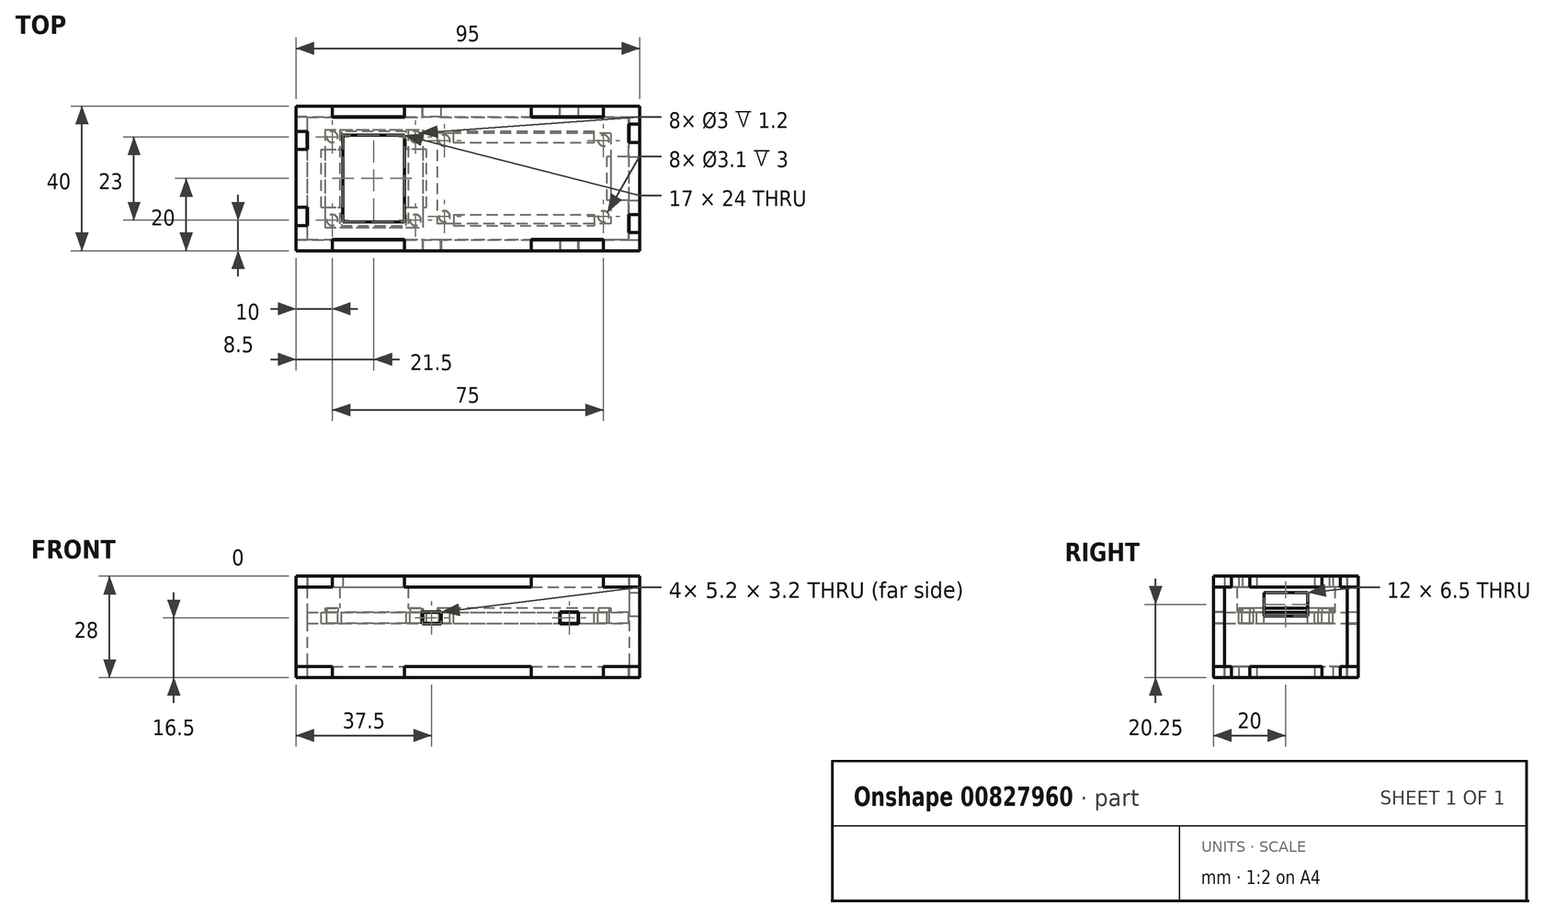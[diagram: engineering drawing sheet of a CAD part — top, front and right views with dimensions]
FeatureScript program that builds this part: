
annotation { "Feature Type Name" : "Feature", "Feature Type Description" : "" }
export const myFeature = defineFeature(function(context is Context, id is Id, definition is map)
    precondition{}
    {
        {
            var Q0;
            Q0=qCreatedBy(makeId("Top.planeOp"),FACE);
            var sketch = newSketch(context, id + "F0", { "sketchPlane" : qUnion([Q0])});
            skLineSegment(sketch, "E0.bottom", {"start": v(24, 12.5) * mm, "end": v(-24, 12.5) * mm});
            skLineSegment(sketch, "E0.top", {"start": v(24, -12.5) * mm, "end": v(-24, -12.5) * mm});
            skLineSegment(sketch, "E0.left", {"start": v(24, 12.5) * mm, "end": v(24, -12.5) * mm});
            skLineSegment(sketch, "E0.right", {"start": v(-24, 12.5) * mm, "end": v(-24, -12.5) * mm});
            skCircle(sketch, "E1", {"center": v(22, 10.5) * mm, "radius": 1.5 * mm});
            skCircle(sketch, "E2.MirrorC", {"center": v(22, -10.5) * mm, "radius": 1.5 * mm});
            skCircle(sketch, "E3.MirrorC", {"center": v(-22, 10.5) * mm, "radius": 1.5 * mm});
            skCircle(sketch, "E4.MirrorC", {"center": v(-22, -10.5) * mm, "radius": 1.5 * mm});
            skSolve(sketch);
        }
        {
            var Q0;
            Q0=makeQuery(id+"F0.imprint","IMPRINT",FACE,{"disambiguationData":[TD([[makeQuery(id+"F0.imprint","IMPRINT",EDGE,{"derivedFrom":sQuery(id+"F0.wireOp",EDGE,"E0.bottom")}),1.0]])]});
            extrude(context, id + "F1", {"entities" : qUnion([Q0]), "depth" : 1.2 * mm, "offsetDistance" : 25 * mm});
        }
        {
            var Q0;
            Q0=qCreatedBy(makeId("Top.planeOp"),FACE);
            cPlane(context, id + "F2", {"entities" : qUnion([Q0]), "cplaneType" : CPlaneType.OFFSET, "offset" : 0 * mm, "width" : 150 * mm, "height" : 150 * mm});
        }
        {
            var Q0;
            Q0=qCreatedBy(id+"F2.planeOp",FACE);
            var sketch = newSketch(context, id + "F3", { "sketchPlane" : qUnion([Q0])});
            skLineSegment(sketch, "E5.bottom", {"start": v(-55, 13.5) * mm, "end": v(-28, 13.5) * mm});
            skLineSegment(sketch, "E5.top", {"start": v(-55, -13.5) * mm, "end": v(-28, -13.5) * mm});
            skLineSegment(sketch, "E5.left", {"start": v(-55, 13.5) * mm, "end": v(-55, -13.5) * mm});
            skLineSegment(sketch, "E5.right", {"start": v(-28, 13.5) * mm, "end": v(-28, -13.5) * mm});
            skCircle(sketch, "E6", {"center": v(-53, 11.5) * mm, "radius": 1.5 * mm});
            skCircle(sketch, "E7", {"center": v(-30, 11.5) * mm, "radius": 1.5 * mm});
            skCircle(sketch, "E8.MirrorC", {"center": v(-53, -11.5) * mm, "radius": 1.5 * mm});
            skCircle(sketch, "E9.MirrorC", {"center": v(-30, -11.5) * mm, "radius": 1.5 * mm});
            skSolve(sketch);
        }
        {
            var Q0;
            Q0=makeQuery(id+"F3.imprint","IMPRINT",FACE,{"disambiguationData":[TD([[makeQuery(id+"F3.imprint","IMPRINT",EDGE,{"derivedFrom":sQuery(id+"F3.wireOp",EDGE,"E5.bottom")}),-1.0]])]});
            extrude(context, id + "F4", {"entities" : qUnion([Q0]), "depth" : 1.2 * mm, "offsetDistance" : 25 * mm});
        }
        {
            var Q0;
            Q0=makeQuery(id+"F4.opExtrude","CAP_FACE",FACE,{"disambiguationData":[OSD([sQuery(id+"F3.wireOp",EDGE,"E5.bottom"),sQuery(id+"F3.wireOp",EDGE,"E5.top"),sQuery(id+"F3.wireOp",EDGE,"E5.left"),sQuery(id+"F3.wireOp",EDGE,"E5.right")])],"isStart":false});
            var sketch = newSketch(context, id + "F5", { "sketchPlane" : qUnion([Q0])});
            skLineSegment(sketch, "E10.bottom", {"start": v(-51, 13.5) * mm, "end": v(-32, 13.5) * mm});
            skLineSegment(sketch, "E10.top", {"start": v(-51, -13.5) * mm, "end": v(-32, -13.5) * mm});
            skLineSegment(sketch, "E10.left", {"start": v(-51, 13.5) * mm, "end": v(-51, -13.5) * mm});
            skLineSegment(sketch, "E10.right", {"start": v(-32, 13.5) * mm, "end": v(-32, -13.5) * mm});
            skSolve(sketch);
        }
        {
            var Q0;
            Q0=makeQuery(id+"F5.imprint","IMPRINT",FACE,{"disambiguationData":[TD([[makeQuery(id+"F5.imprint","IMPRINT",EDGE,{"derivedFrom":sQuery(id+"F5.wireOp",EDGE,"E10.bottom")}),-1.0]])]});
            extrude(context, id + "F6", {"entities" : qUnion([Q0]), "operationType" : NewBodyOperationType.ADD, "depth" : 5.8 * mm, "offsetDistance" : 25 * mm});
        }
        {
            var Q0;
            Q0=makeQuery(id+"F6.opExtrude","CAP_FACE",FACE,{"disambiguationData":[OSD([sQuery(id+"F5.wireOp",EDGE,"E10.bottom"),sQuery(id+"F5.wireOp",EDGE,"E10.top"),sQuery(id+"F5.wireOp",EDGE,"E10.left"),sQuery(id+"F5.wireOp",EDGE,"E10.right")])],"isStart":false});
            var sketch = newSketch(context, id + "F7", { "sketchPlane" : qUnion([Q0])});
            skLineSegment(sketch, "E11.bottom", {"start": v(-63, 20) * mm, "end": v(-53, 20) * mm});
            skLineSegment(sketch, "E11.top", {"start": v(-63, -20) * mm, "end": v(-53, -20) * mm});
            skLineSegment(sketch, "E11.left", {"start": v(-63, 20) * mm, "end": v(-63, 13) * mm});
            skLineSegment(sketch, "E11.right", {"start": v(32, 20) * mm, "end": v(32, 15) * mm});
            skLineSegment(sketch, "E12.top", {"start": v(-53, 16.9) * mm, "end": v(-33, 16.9) * mm});
            skLineSegment(sketch, "E12.left", {"start": v(-53, 20) * mm, "end": v(-53, 16.9) * mm});
            skLineSegment(sketch, "E12.right", {"start": v(-33, 20) * mm, "end": v(-33, 16.9) * mm});
            skLineSegment(sketch, "E13.top", {"start": v(2, 16.9) * mm, "end": v(22, 16.9) * mm});
            skLineSegment(sketch, "E13.left", {"start": v(2, 20) * mm, "end": v(2, 16.9) * mm});
            skLineSegment(sketch, "E13.right", {"start": v(22, 20) * mm, "end": v(22, 16.9) * mm});
            skLineSegment(sketch, "E14.trimOffspring", {"start": v(-33, 20) * mm, "end": v(2, 20) * mm});
            skLineSegment(sketch, "E15.trimOffspring", {"start": v(22, 20) * mm, "end": v(32, 20) * mm});
            skLineSegment(sketch, "E16.MirrorCS", {"start": v(22, -20) * mm, "end": v(22, -16.9) * mm});
            skLineSegment(sketch, "E17.MirrorCS", {"start": v(2, -16.9) * mm, "end": v(22, -16.9) * mm});
            skLineSegment(sketch, "E18.MirrorCS", {"start": v(2, -20) * mm, "end": v(2, -16.9) * mm});
            skLineSegment(sketch, "E19.MirrorCS", {"start": v(-53, -20) * mm, "end": v(-53, -16.9) * mm});
            skLineSegment(sketch, "E20.MirrorCS", {"start": v(-53, -16.9) * mm, "end": v(-33, -16.9) * mm});
            skLineSegment(sketch, "E21.MirrorCS", {"start": v(-33, -20) * mm, "end": v(-33, -16.9) * mm});
            skLineSegment(sketch, "E22.trimOffspring", {"start": v(22, -20) * mm, "end": v(32, -20) * mm});
            skLineSegment(sketch, "E23.trimOffspring", {"start": v(-33, -20) * mm, "end": v(2, -20) * mm});
            skLineSegment(sketch, "E24.bottom", {"start": v(-63, 13) * mm, "end": v(-59.9, 13) * mm});
            skLineSegment(sketch, "E24.top", {"start": v(-63, 8) * mm, "end": v(-59.9, 8) * mm});
            skLineSegment(sketch, "E24.right", {"start": v(-59.9, 13) * mm, "end": v(-59.9, 8) * mm});
            skLineSegment(sketch, "E25.MirrorCS", {"start": v(-63, -8) * mm, "end": v(-59.9, -8) * mm});
            skLineSegment(sketch, "E26.MirrorCS", {"start": v(-59.9, -13) * mm, "end": v(-59.9, -8) * mm});
            skLineSegment(sketch, "E27.MirrorCS", {"start": v(-63, -13) * mm, "end": v(-59.9, -13) * mm});
            skLineSegment(sketch, "E28.trimOffspring", {"start": v(-63, -13) * mm, "end": v(-63, -20) * mm});
            skLineSegment(sketch, "E29.trimOffspring", {"start": v(-63, 8) * mm, "end": v(-63, -8) * mm});
            skLineSegment(sketch, "E30.bottom", {"start": v(32, 15) * mm, "end": v(28.9, 15) * mm});
            skLineSegment(sketch, "E30.top", {"start": v(32, 10) * mm, "end": v(28.9, 10) * mm});
            skLineSegment(sketch, "E30.right", {"start": v(28.9, 15) * mm, "end": v(28.9, 10) * mm});
            skLineSegment(sketch, "E31.trimOffspring", {"start": v(32, 10) * mm, "end": v(32, -10) * mm});
            skLineSegment(sketch, "E32.MirrorCS", {"start": v(32, -10) * mm, "end": v(28.9, -10) * mm});
            skLineSegment(sketch, "E33.MirrorCS", {"start": v(28.9, -15) * mm, "end": v(28.9, -10) * mm});
            skLineSegment(sketch, "E34.MirrorCS", {"start": v(32, -15) * mm, "end": v(28.9, -15) * mm});
            skLineSegment(sketch, "E35.trimOffspring", {"start": v(32, -15) * mm, "end": v(32, -20) * mm});
            skLineSegment(sketch, "E36.bottom", {"start": v(-50, 12) * mm, "end": v(-33, 12) * mm});
            skLineSegment(sketch, "E36.top", {"start": v(-50, -12) * mm, "end": v(-33, -12) * mm});
            skLineSegment(sketch, "E36.left", {"start": v(-50, 12) * mm, "end": v(-50, -12) * mm});
            skLineSegment(sketch, "E36.right", {"start": v(-33, 12) * mm, "end": v(-33, -12) * mm});
            skSolve(sketch);
        }
        {
            var Q0;
            Q0 = qSketchRegion(id + "F7", true);
            extrude(context, id + "F8", {"entities" : qUnion([Q0]), "depth" : 3 * mm, "offsetDistance" : 25 * mm});
        }
        {
            var Q0;
            Q0=qCreatedBy(makeId("Top.planeOp"),FACE);
            var sketch = newSketch(context, id + "F9", { "sketchPlane" : qUnion([Q0])});
            skLineSegment(sketch, "E37.bottom", {"start": v(-59.9, -16.9) * mm, "end": v(-28, -16.9) * mm});
            skLineSegment(sketch, "E37.top", {"start": v(-59.9, 16.9) * mm, "end": v(-28, 16.9) * mm});
            skLineSegment(sketch, "E37.left", {"start": v(-59.9, -16.9) * mm, "end": v(-59.9, 16.9) * mm});
            skLineSegment(sketch, "E37.right", {"start": v(28.9, -16.9) * mm, "end": v(28.9, -6) * mm});
            skLineSegment(sketch, "E38", {"start": v(-19.45, -10) * mm, "end": v(-19.45, -13) * mm});
            skCircle(sketch, "E39", {"center": v(-22, -10.5) * mm, "radius": 1.55 * mm});
            skCircle(sketch, "E40.MirrorC", {"center": v(-22, 10.5) * mm, "radius": 1.55 * mm});
            skLineSegment(sketch, "E41.MirrorCS", {"start": v(-19.45, 10) * mm, "end": v(-19.45, 13) * mm});
            skLineSegment(sketch, "E42.MirrorCS", {"start": v(19.45, -10) * mm, "end": v(19.45, -13) * mm});
            skCircle(sketch, "E43.MirrorC", {"center": v(22, -10.5) * mm, "radius": 1.55 * mm});
            skLineSegment(sketch, "E44.MirrorCS", {"start": v(19.45, 10) * mm, "end": v(19.45, 13) * mm});
            skCircle(sketch, "E45.MirrorC", {"center": v(22, 10.5) * mm, "radius": 1.55 * mm});
            skLineSegment(sketch, "E46", {"start": v(-19.45, -10) * mm, "end": v(19.45, -10) * mm});
            skLineSegment(sketch, "E47", {"start": v(-19.45, -13) * mm, "end": v(19.45, -13) * mm});
            skLineSegment(sketch, "E48", {"start": v(-19.45, 10) * mm, "end": v(19.45, 10) * mm});
            skLineSegment(sketch, "E49", {"start": v(19.45, 13) * mm, "end": v(-19.45, 13) * mm});
            skLineSegment(sketch, "E50.bottom", {"start": v(28.9, -6) * mm, "end": v(23, -6) * mm});
            skLineSegment(sketch, "E50.top", {"start": v(28.9, 6) * mm, "end": v(23, 6) * mm});
            skLineSegment(sketch, "E50.right", {"start": v(23, -6) * mm, "end": v(23, 6) * mm});
            skLineSegment(sketch, "E51.trimOffspring", {"start": v(28.9, 6) * mm, "end": v(28.9, 16.9) * mm});
            skCircle(sketch, "E52", {"center": v(-53, -11.5) * mm, "radius": 1.55 * mm});
            skCircle(sketch, "E53", {"center": v(-30, -11.5) * mm, "radius": 1.55 * mm});
            skCircle(sketch, "E54.MirrorC", {"center": v(-30, 11.5) * mm, "radius": 1.55 * mm});
            skCircle(sketch, "E55.MirrorC", {"center": v(-53, 11.5) * mm, "radius": 1.55 * mm});
            skLineSegment(sketch, "E56.bottom", {"start": v(-56, -8) * mm, "end": v(-50.5, -8) * mm});
            skLineSegment(sketch, "E56.top", {"start": v(-56, 8) * mm, "end": v(-50.5, 8) * mm});
            skLineSegment(sketch, "E56.left", {"start": v(-56, -8) * mm, "end": v(-56, 8) * mm});
            skLineSegment(sketch, "E57", {"start": v(-50.5, -8) * mm, "end": v(-50.5, -13) * mm});
            skLineSegment(sketch, "E58", {"start": v(-50.5, -13) * mm, "end": v(-32.5, -13) * mm});
            skLineSegment(sketch, "E59", {"start": v(-32.5, -13) * mm, "end": v(-32.5, -8) * mm});
            skLineSegment(sketch, "E60", {"start": v(-32.5, -8) * mm, "end": v(-27, -8) * mm});
            skLineSegment(sketch, "E61", {"start": v(-27, -8) * mm, "end": v(-27, 8) * mm});
            skLineSegment(sketch, "E62", {"start": v(-27, 8) * mm, "end": v(-32.5, 8) * mm});
            skLineSegment(sketch, "E63", {"start": v(-32.5, 8) * mm, "end": v(-32.5, 13) * mm});
            skLineSegment(sketch, "E64", {"start": v(-32.5, 13) * mm, "end": v(-50.5, 13) * mm});
            skLineSegment(sketch, "E65", {"start": v(-50.5, 13) * mm, "end": v(-50.5, 8) * mm});
            skLineSegment(sketch, "E66", {"start": v(-28, -16.9) * mm, "end": v(-28, -20) * mm});
            skLineSegment(sketch, "E67", {"start": v(-28, -20) * mm, "end": v(-23, -20) * mm});
            skLineSegment(sketch, "E68", {"start": v(-23, -20) * mm, "end": v(-23, -16.9) * mm});
            skLineSegment(sketch, "E69", {"start": v(10, -16.9) * mm, "end": v(10, -20) * mm});
            skLineSegment(sketch, "E70", {"start": v(10, -20) * mm, "end": v(15, -20) * mm});
            skLineSegment(sketch, "E71", {"start": v(15, -20) * mm, "end": v(15, -16.9) * mm});
            skLineSegment(sketch, "E72.MirrorCS", {"start": v(10, 16.9) * mm, "end": v(10, 20) * mm});
            skLineSegment(sketch, "E73.MirrorCS", {"start": v(10, 20) * mm, "end": v(15, 20) * mm});
            skLineSegment(sketch, "E74.MirrorCS", {"start": v(15, 20) * mm, "end": v(15, 16.9) * mm});
            skLineSegment(sketch, "E75.MirrorCS", {"start": v(-28, 20) * mm, "end": v(-23, 20) * mm});
            skLineSegment(sketch, "E76.MirrorCS", {"start": v(-28, 16.9) * mm, "end": v(-28, 20) * mm});
            skLineSegment(sketch, "E77.MirrorCS", {"start": v(-23, 20) * mm, "end": v(-23, 16.9) * mm});
            skLineSegment(sketch, "E78.trimOffspring", {"start": v(-23, -16.9) * mm, "end": v(10, -16.9) * mm});
            skLineSegment(sketch, "E79.trimOffspring", {"start": v(15, -16.9) * mm, "end": v(28.9, -16.9) * mm});
            skLineSegment(sketch, "E80.trimOffspring", {"start": v(-23, 16.9) * mm, "end": v(10, 16.9) * mm});
            skLineSegment(sketch, "E81.trimOffspring", {"start": v(15, 16.9) * mm, "end": v(28.9, 16.9) * mm});
            skSolve(sketch);
        }
        {
            var Q0;
            Q0=makeQuery(id+"F9.imprint","IMPRINT",FACE,{"disambiguationData":[TD([[makeQuery(id+"F9.imprint","IMPRINT",EDGE,{"derivedFrom":sQuery(id+"F9.wireOp",EDGE,"E37.bottom")}),1.0]])]});
            extrude(context, id + "F10", {"entities" : qUnion([Q0]), "operationType" : NewBodyOperationType.ADD, "oppositeDirection" : true, "depth" : 3 * mm, "offsetDistance" : 25 * mm});
        }
        {
            var Q0;
            Q0=qCreatedBy(makeId("Top.planeOp"),FACE);
            cPlane(context, id + "F11", {"entities" : qUnion([Q0]), "cplaneType" : CPlaneType.OFFSET, "offset" : 15 * mm, "oppositeDirection" : true, "width" : 150 * mm, "height" : 150 * mm});
        }
        {
            var Q0;
            Q0=qCreatedBy(id+"F11.planeOp",FACE);
            var sketch = newSketch(context, id + "F12", { "sketchPlane" : qUnion([Q0])});
            skLineSegment(sketch, "E82.0.0", {"start": v(22, -20) * mm, "end": v(22, -16.9) * mm});
            skLineSegment(sketch, "E82.0.1", {"start": v(22, -16.9) * mm, "end": v(2, -16.9) * mm});
            skLineSegment(sketch, "E82.0.2", {"start": v(2, -16.9) * mm, "end": v(2, -20) * mm});
            skLineSegment(sketch, "E82.0.3", {"start": v(2, -20) * mm, "end": v(-33, -20) * mm});
            skLineSegment(sketch, "E82.0.4", {"start": v(-33, -20) * mm, "end": v(-33, -16.9) * mm});
            skLineSegment(sketch, "E82.0.5", {"start": v(-33, -16.9) * mm, "end": v(-53, -16.9) * mm});
            skLineSegment(sketch, "E82.0.6", {"start": v(-53, -16.9) * mm, "end": v(-53, -20) * mm});
            skLineSegment(sketch, "E82.0.7", {"start": v(-53, -20) * mm, "end": v(-63, -20) * mm});
            skLineSegment(sketch, "E82.0.8", {"start": v(-63, -20) * mm, "end": v(-63, -13) * mm});
            skLineSegment(sketch, "E82.0.9", {"start": v(-63, -13) * mm, "end": v(-59.9, -13) * mm});
            skLineSegment(sketch, "E82.0.10", {"start": v(-59.9, -13) * mm, "end": v(-59.9, -8) * mm});
            skLineSegment(sketch, "E82.0.11", {"start": v(-59.9, -8) * mm, "end": v(-63, -8) * mm});
            skLineSegment(sketch, "E82.0.12", {"start": v(-63, -8) * mm, "end": v(-63, 8) * mm});
            skLineSegment(sketch, "E82.0.13", {"start": v(-63, 8) * mm, "end": v(-59.9, 8) * mm});
            skLineSegment(sketch, "E82.0.14", {"start": v(-59.9, 8) * mm, "end": v(-59.9, 13) * mm});
            skLineSegment(sketch, "E82.0.15", {"start": v(-59.9, 13) * mm, "end": v(-63, 13) * mm});
            skLineSegment(sketch, "E82.0.16", {"start": v(-63, 13) * mm, "end": v(-63, 20) * mm});
            skLineSegment(sketch, "E82.0.17", {"start": v(-63, 20) * mm, "end": v(-53, 20) * mm});
            skLineSegment(sketch, "E82.0.18", {"start": v(-53, 20) * mm, "end": v(-53, 16.9) * mm});
            skLineSegment(sketch, "E82.0.19", {"start": v(-53, 16.9) * mm, "end": v(-33, 16.9) * mm});
            skLineSegment(sketch, "E82.0.20", {"start": v(-33, 16.9) * mm, "end": v(-33, 20) * mm});
            skLineSegment(sketch, "E82.0.21", {"start": v(-33, 20) * mm, "end": v(2, 20) * mm});
            skLineSegment(sketch, "E82.0.22", {"start": v(2, 20) * mm, "end": v(2, 16.9) * mm});
            skLineSegment(sketch, "E82.0.23", {"start": v(2, 16.9) * mm, "end": v(22, 16.9) * mm});
            skLineSegment(sketch, "E82.0.24", {"start": v(22, 16.9) * mm, "end": v(22, 20) * mm});
            skLineSegment(sketch, "E82.0.25", {"start": v(22, 20) * mm, "end": v(32, 20) * mm});
            skLineSegment(sketch, "E82.0.26", {"start": v(32, 20) * mm, "end": v(32, 15) * mm});
            skLineSegment(sketch, "E82.0.27", {"start": v(32, 15) * mm, "end": v(28.9, 15) * mm});
            skLineSegment(sketch, "E82.0.28", {"start": v(28.9, 15) * mm, "end": v(28.9, 10) * mm});
            skLineSegment(sketch, "E82.0.29", {"start": v(28.9, 10) * mm, "end": v(32, 10) * mm});
            skLineSegment(sketch, "E82.0.30", {"start": v(32, 10) * mm, "end": v(32, -10) * mm});
            skLineSegment(sketch, "E82.0.31", {"start": v(32, -10) * mm, "end": v(28.9, -10) * mm});
            skLineSegment(sketch, "E82.0.32", {"start": v(28.9, -10) * mm, "end": v(28.9, -15) * mm});
            skLineSegment(sketch, "E82.0.33", {"start": v(28.9, -15) * mm, "end": v(32, -15) * mm});
            skLineSegment(sketch, "E82.0.34", {"start": v(32, -15) * mm, "end": v(32, -20) * mm});
            skLineSegment(sketch, "E82.0.35", {"start": v(32, -20) * mm, "end": v(22, -20) * mm});
            skSolve(sketch);
        }
        {
            var Q0;
            Q0=makeQuery(id+"F12.imprint","IMPRINT",FACE,{"disambiguationData":[TD([[makeQuery(id+"F12.imprint","IMPRINT",EDGE,{"derivedFrom":sQuery(id+"F12.wireOp",EDGE,"E82.0.0")}),-1.0]])]});
            extrude(context, id + "F13", {"entities" : qUnion([Q0]), "oppositeDirection" : true, "depth" : 3 * mm, "offsetDistance" : 25 * mm});
        }
        {
            var Q0;
            Q0=makeQuery(id+"F8.opExtrude","SWEPT_FACE",FACE,{"disambiguationData":[OSD([sQuery(id+"F7.wireOp",EDGE,"E11.top")])]});
            var sketch = newSketch(context, id + "F14", { "sketchPlane" : qUnion([Q0])});
            skLineSegment(sketch, "E83.bottom", {"start": v(-53, 10) * mm, "end": v(-33, 10) * mm});
            skLineSegment(sketch, "E83.top", {"start": v(-53, -18) * mm, "end": v(-33, -18) * mm});
            skLineSegment(sketch, "E83.left", {"start": v(-63, 7) * mm, "end": v(-63, -15) * mm});
            skLineSegment(sketch, "E83.right", {"start": v(32, 7) * mm, "end": v(32, -15) * mm});
            skLineSegment(sketch, "E84", {"start": v(-53, 10) * mm, "end": v(-53, 7) * mm});
            skLineSegment(sketch, "E85", {"start": v(-53, 7) * mm, "end": v(-63, 7) * mm});
            skLineSegment(sketch, "E86.top", {"start": v(-33, 7) * mm, "end": v(2, 7) * mm});
            skLineSegment(sketch, "E86.left", {"start": v(-33, 10) * mm, "end": v(-33, 7) * mm});
            skLineSegment(sketch, "E86.right", {"start": v(2, 10) * mm, "end": v(2, 7) * mm});
            skLineSegment(sketch, "E87.trimOffspring", {"start": v(2, 10) * mm, "end": v(22, 10) * mm});
            skLineSegment(sketch, "E88", {"start": v(22, 10) * mm, "end": v(22, 7) * mm});
            skLineSegment(sketch, "E89", {"start": v(22, 7) * mm, "end": v(32, 7) * mm});
            skLineSegment(sketch, "E90", {"start": v(-63, -15) * mm, "end": v(-53, -15) * mm});
            skLineSegment(sketch, "E91", {"start": v(-53, -15) * mm, "end": v(-53, -18) * mm});
            skLineSegment(sketch, "E92.top", {"start": v(-33, -15) * mm, "end": v(2, -15) * mm});
            skLineSegment(sketch, "E92.left", {"start": v(-33, -18) * mm, "end": v(-33, -15) * mm});
            skLineSegment(sketch, "E92.right", {"start": v(2, -18) * mm, "end": v(2, -15) * mm});
            skLineSegment(sketch, "E93", {"start": v(22, -18) * mm, "end": v(22, -15) * mm});
            skLineSegment(sketch, "E94", {"start": v(22, -15) * mm, "end": v(32, -15) * mm});
            skLineSegment(sketch, "E95.trimOffspring", {"start": v(2, -18) * mm, "end": v(22, -18) * mm});
            skLineSegment(sketch, "E96.0", {"start": v(-22.9, 0.1) * mm, "end": v(-28.1, 0.1) * mm});
            skLineSegment(sketch, "E96.1", {"start": v(-22.9, -3.1) * mm, "end": v(-22.9, 0.1) * mm});
            skLineSegment(sketch, "E96.2", {"start": v(-28.1, -3.1) * mm, "end": v(-22.9, -3.1) * mm});
            skLineSegment(sketch, "E96.3", {"start": v(-28.1, 0.1) * mm, "end": v(-28.1, -3.1) * mm});
            skLineSegment(sketch, "E97.0", {"start": v(15.1, 0.1) * mm, "end": v(9.9, 0.1) * mm});
            skLineSegment(sketch, "E97.1", {"start": v(15.1, -3.1) * mm, "end": v(15.1, 0.1) * mm});
            skLineSegment(sketch, "E97.2", {"start": v(9.9, -3.1) * mm, "end": v(15.1, -3.1) * mm});
            skLineSegment(sketch, "E97.3", {"start": v(9.9, 0.1) * mm, "end": v(9.9, -3.1) * mm});
            skSolve(sketch);
        }
        {
            var Q0;
            Q0=makeQuery(id+"F14.imprint","IMPRINT",FACE,{"disambiguationData":[TD([[makeQuery(id+"F14.imprint","IMPRINT",EDGE,{"derivedFrom":sQuery(id+"F14.wireOp",EDGE,"E83.bottom")}),-1.0]])]});
            extrude(context, id + "F15", {"entities" : qUnion([Q0]), "oppositeDirection" : true, "depth" : 3 * mm, "offsetDistance" : 25 * mm});
        }
        {
            var Q0;
            Q0=makeQuery(id+"F8.opExtrude","SWEPT_FACE",FACE,{"disambiguationData":[OSD([sQuery(id+"F7.wireOp",EDGE,"E31.trimOffspring")])]});
            var sketch = newSketch(context, id + "F16", { "sketchPlane" : qUnion([Q0])});
            skLineSegment(sketch, "E98.bottom", {"start": v(-17, 7) * mm, "end": v(-15, 7) * mm});
            skLineSegment(sketch, "E98.top", {"start": v(-17, -15) * mm, "end": v(-15, -15) * mm});
            skLineSegment(sketch, "E98.left", {"start": v(-17, 7) * mm, "end": v(-17, -15) * mm});
            skLineSegment(sketch, "E99.bottom", {"start": v(-15, 10) * mm, "end": v(-10, 10) * mm});
            skLineSegment(sketch, "E99.left", {"start": v(-15, 10) * mm, "end": v(-15, 7) * mm});
            skLineSegment(sketch, "E99.right", {"start": v(-10, 10) * mm, "end": v(-10, 7) * mm});
            skLineSegment(sketch, "E100.top", {"start": v(-15, -18) * mm, "end": v(-10, -18) * mm});
            skLineSegment(sketch, "E100.left", {"start": v(-15, -15) * mm, "end": v(-15, -18) * mm});
            skLineSegment(sketch, "E100.right", {"start": v(-10, -15) * mm, "end": v(-10, -18) * mm});
            skLineSegment(sketch, "E101.MirrorCS", {"start": v(10, 10) * mm, "end": v(10, 7) * mm});
            skLineSegment(sketch, "E102.MirrorCS", {"start": v(15, 10) * mm, "end": v(10, 10) * mm});
            skLineSegment(sketch, "E103.MirrorCS", {"start": v(15, 10) * mm, "end": v(15, 7) * mm});
            skLineSegment(sketch, "E104.MirrorCS", {"start": v(17, 7) * mm, "end": v(15, 7) * mm});
            skLineSegment(sketch, "E105.MirrorCS", {"start": v(17, 7) * mm, "end": v(17, -15) * mm});
            skLineSegment(sketch, "E106.MirrorCS", {"start": v(17, -15) * mm, "end": v(15, -15) * mm});
            skLineSegment(sketch, "E107.MirrorCS", {"start": v(15, -15) * mm, "end": v(15, -18) * mm});
            skLineSegment(sketch, "E108.MirrorCS", {"start": v(15, -18) * mm, "end": v(10, -18) * mm});
            skLineSegment(sketch, "E109.MirrorCS", {"start": v(10, -15) * mm, "end": v(10, -18) * mm});
            skLineSegment(sketch, "E110", {"start": v(-10, -15) * mm, "end": v(10, -15) * mm});
            skLineSegment(sketch, "E111", {"start": v(-10, 7) * mm, "end": v(10, 7) * mm});
            skLineSegment(sketch, "E112.bottom", {"start": v(-6, 5.5) * mm, "end": v(6, 5.5) * mm});
            skLineSegment(sketch, "E112.top", {"start": v(-6, -1) * mm, "end": v(6, -1) * mm});
            skLineSegment(sketch, "E112.left", {"start": v(-6, 5.5) * mm, "end": v(-6, -1) * mm});
            skLineSegment(sketch, "E112.right", {"start": v(6, 5.5) * mm, "end": v(6, -1) * mm});
            skSolve(sketch);
        }
        {
            var Q0;
            Q0=makeQuery(id+"F16.imprint","IMPRINT",FACE,{"disambiguationData":[TD([[makeQuery(id+"F16.imprint","IMPRINT",EDGE,{"derivedFrom":sQuery(id+"F16.wireOp",EDGE,"E98.bottom")}),-1.0]])]});
            extrude(context, id + "F17", {"entities" : qUnion([Q0]), "oppositeDirection" : true, "depth" : 3 * mm, "offsetDistance" : 25 * mm});
        }
        {
            var Q0;
            Q0=makeQuery(id+"F8.opExtrude","SWEPT_FACE",FACE,{"disambiguationData":[OSD([sQuery(id+"F7.wireOp",EDGE,"E29.trimOffspring")])]});
            var sketch = newSketch(context, id + "F18", { "sketchPlane" : qUnion([Q0])});
            skLineSegment(sketch, "E113.0.2", {"start": v(-17, 7) * mm, "end": v(-17, -15) * mm});
            skLineSegment(sketch, "E113.0.12", {"start": v(17, -15) * mm, "end": v(17, 7) * mm});
            skLineSegment(sketch, "E114", {"start": v(-17, 7) * mm, "end": v(-13, 7) * mm});
            skLineSegment(sketch, "E115.bottom", {"start": v(-13, 10) * mm, "end": v(-8, 10) * mm});
            skLineSegment(sketch, "E115.left", {"start": v(-13, 10) * mm, "end": v(-13, 7) * mm});
            skLineSegment(sketch, "E115.right", {"start": v(-8, 10) * mm, "end": v(-8, 7) * mm});
            skLineSegment(sketch, "E116.bottom", {"start": v(8, 10) * mm, "end": v(13, 10) * mm});
            skLineSegment(sketch, "E116.left", {"start": v(8, 10) * mm, "end": v(8, 7) * mm});
            skLineSegment(sketch, "E116.right", {"start": v(13, 10) * mm, "end": v(13, 7) * mm});
            skLineSegment(sketch, "E117", {"start": v(-17, -15) * mm, "end": v(-13, -15) * mm});
            skLineSegment(sketch, "E118.top", {"start": v(-13, -18) * mm, "end": v(-8, -18) * mm});
            skLineSegment(sketch, "E118.left", {"start": v(-13, -15) * mm, "end": v(-13, -18) * mm});
            skLineSegment(sketch, "E118.right", {"start": v(-8, -15) * mm, "end": v(-8, -18) * mm});
            skLineSegment(sketch, "E119.top", {"start": v(8, -18) * mm, "end": v(13, -18) * mm});
            skLineSegment(sketch, "E119.left", {"start": v(8, -15) * mm, "end": v(8, -18) * mm});
            skLineSegment(sketch, "E119.right", {"start": v(13, -15) * mm, "end": v(13, -18) * mm});
            skLineSegment(sketch, "E120.trimOffspring", {"start": v(-8, -15) * mm, "end": v(8, -15) * mm});
            skLineSegment(sketch, "E121.trimOffspring", {"start": v(13, -15) * mm, "end": v(17, -15) * mm});
            skLineSegment(sketch, "E122.trimOffspring", {"start": v(-8, 7) * mm, "end": v(8, 7) * mm});
            skLineSegment(sketch, "E123.trimOffspring", {"start": v(13, 7) * mm, "end": v(17, 7) * mm});
            skSolve(sketch);
        }
        {
            var Q0;
            Q0=makeQuery(id+"F18.imprint","IMPRINT",FACE,{"disambiguationData":[TD([[makeQuery(id+"F18.imprint","IMPRINT",EDGE,{"derivedFrom":sQuery(id+"F18.wireOp",EDGE,"E113.0.2")}),1.0]])]});
            extrude(context, id + "F19", {"entities" : qUnion([Q0]), "oppositeDirection" : true, "depth" : 3 * mm, "offsetDistance" : 25 * mm});
        }
        {
            var Q0;
            Q0=makeQuery(id+"F15.opExtrude","SWEPT_BODY",BODY,{"disambiguationData":[OSD([sQuery(id+"F14.wireOp",EDGE,"E83.bottom"),sQuery(id+"F14.wireOp",EDGE,"E83.top"),sQuery(id+"F14.wireOp",EDGE,"E83.left"),sQuery(id+"F14.wireOp",EDGE,"E83.right"),sQuery(id+"F14.wireOp",EDGE,"E84"),sQuery(id+"F14.wireOp",EDGE,"E85"),sQuery(id+"F14.wireOp",EDGE,"E86.top"),sQuery(id+"F14.wireOp",EDGE,"E86.left"),sQuery(id+"F14.wireOp",EDGE,"E86.right"),sQuery(id+"F14.wireOp",EDGE,"E87.trimOffspring"),sQuery(id+"F14.wireOp",EDGE,"E88"),sQuery(id+"F14.wireOp",EDGE,"E89"),sQuery(id+"F14.wireOp",EDGE,"E90"),sQuery(id+"F14.wireOp",EDGE,"E91"),sQuery(id+"F14.wireOp",EDGE,"E92.top"),sQuery(id+"F14.wireOp",EDGE,"E92.left"),sQuery(id+"F14.wireOp",EDGE,"E92.right"),sQuery(id+"F14.wireOp",EDGE,"E93"),sQuery(id+"F14.wireOp",EDGE,"E94"),sQuery(id+"F14.wireOp",EDGE,"E95.trimOffspring"),sQuery(id+"F14.wireOp",EDGE,"E96.0"),sQuery(id+"F14.wireOp",EDGE,"E96.1"),sQuery(id+"F14.wireOp",EDGE,"E96.2"),sQuery(id+"F14.wireOp",EDGE,"E96.3"),sQuery(id+"F14.wireOp",EDGE,"E97.0"),sQuery(id+"F14.wireOp",EDGE,"E97.1"),sQuery(id+"F14.wireOp",EDGE,"E97.2"),sQuery(id+"F14.wireOp",EDGE,"E97.3")])]});
            var Q1;
            Q1=qCreatedBy(makeId("Front.planeOp"),FACE);
            mirror(context, id + "F20", {"entities" : qUnion([Q0]), "mirrorPlane" : qUnion([Q1])});
        }
    });
